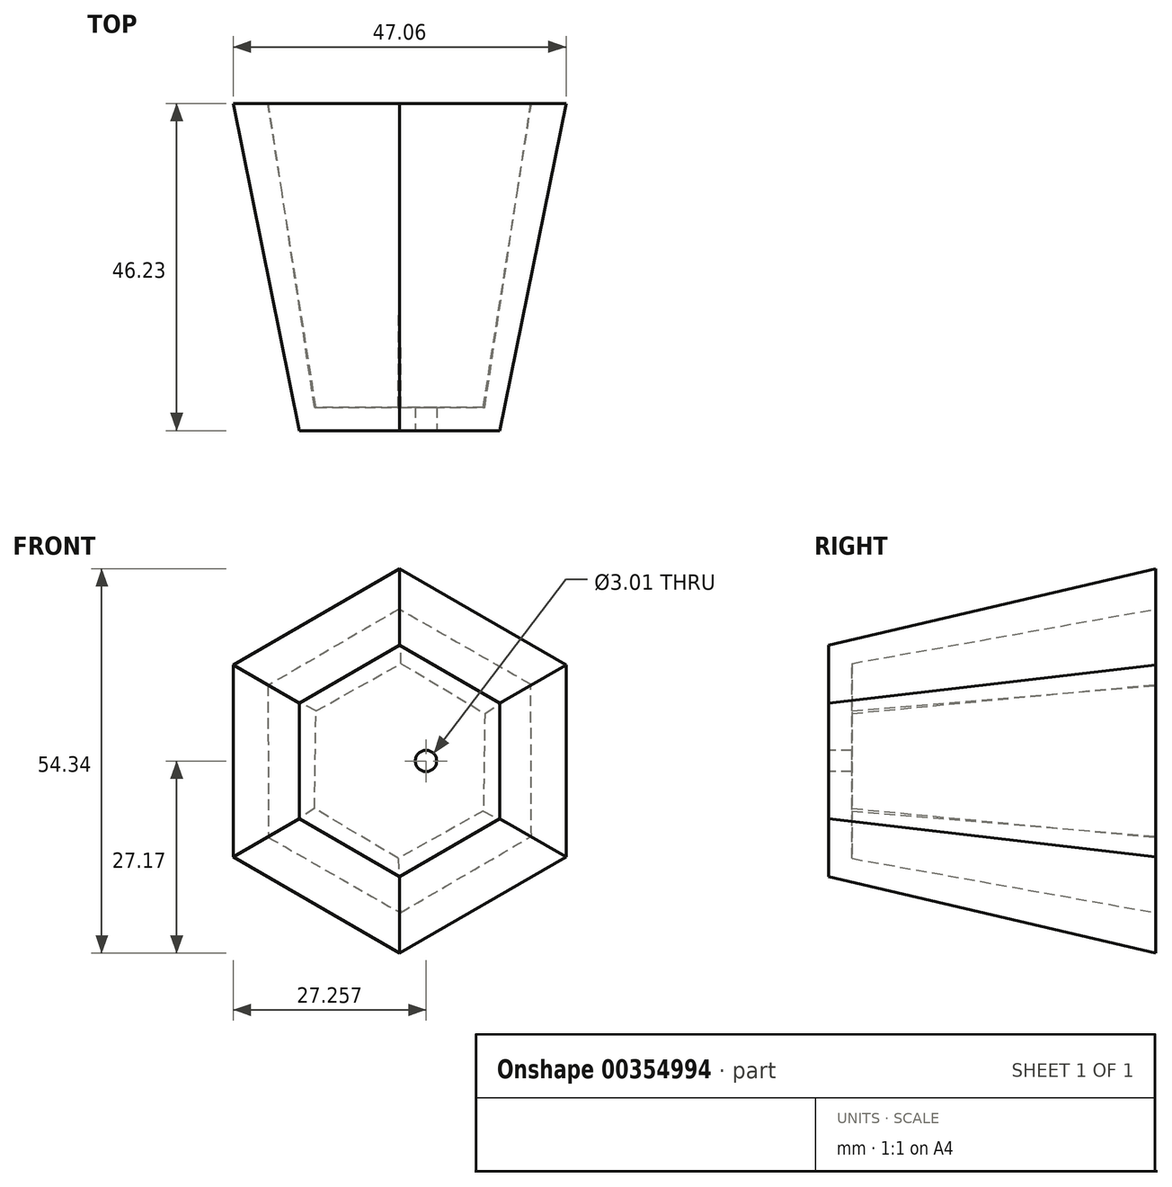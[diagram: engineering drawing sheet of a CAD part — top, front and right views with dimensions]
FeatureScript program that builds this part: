
annotation { "Feature Type Name" : "Feature", "Feature Type Description" : "" }
export const myFeature = defineFeature(function(context is Context, id is Id, definition is map)
    precondition{}
    {
        {
            var Q0;
            Q0=qCreatedBy(makeId("Front.planeOp"),FACE);
            var sketch = newSketch(context, id + "F0", { "sketchPlane" : qUnion([Q0])});
            skCircle(sketch, "E0.cCircle", {"center": v(0, 0) * mm, "radius": 23.53 * mm, "construction": true});
            skLineSegment(sketch, "E0.0", {"start": v(-23.53, -13.58) * mm, "end": v(-23.53, 13.58) * mm});
            skLineSegment(sketch, "E0.1", {"start": v(-23.53, 13.58) * mm, "end": v(0, 27.17) * mm});
            skLineSegment(sketch, "E0.2", {"start": v(0, 27.17) * mm, "end": v(23.53, 13.58) * mm});
            skLineSegment(sketch, "E0.3", {"start": v(23.53, 13.58) * mm, "end": v(23.53, -13.58) * mm});
            skLineSegment(sketch, "E0.4", {"start": v(23.53, -13.58) * mm, "end": v(0, -27.17) * mm});
            skLineSegment(sketch, "E0.5", {"start": v(0, -27.17) * mm, "end": v(-23.53, -13.58) * mm});
            skPoint(sketch, "E0.0.midPoint", {"position": v(-23.53, 0) * mm});
            skPoint(sketch, "E1.0.midPoint", {"position": v(-19.42, 0) * mm});
            skSolve(sketch);
        }
        {
            var Q0;
            Q0=qCreatedBy(makeId("Front.planeOp"),FACE);
            cPlane(context, id + "F1", {"entities" : qUnion([Q0]), "cplaneType" : CPlaneType.OFFSET, "offset" : 46.23 * mm, "width" : 152.4 * mm, "height" : 152.4 * mm});
        }
        {
            var Q0;
            Q0=qCreatedBy(id+"F1.planeOp",FACE);
            var sketch = newSketch(context, id + "F2", { "sketchPlane" : qUnion([Q0])});
            skCircle(sketch, "E2.cCircle", {"center": v(0, 0) * mm, "radius": 14.16 * mm, "construction": true});
            skLineSegment(sketch, "E2.0", {"start": v(0, 16.35) * mm, "end": v(14.17, 8.17) * mm});
            skLineSegment(sketch, "E2.1", {"start": v(14.17, 8.17) * mm, "end": v(14.16, -8.18) * mm});
            skLineSegment(sketch, "E2.2", {"start": v(14.16, -8.18) * mm, "end": v(0, -16.35) * mm});
            skLineSegment(sketch, "E2.3", {"start": v(0, -16.35) * mm, "end": v(-14.17, -8.17) * mm});
            skLineSegment(sketch, "E2.4", {"start": v(-14.17, -8.17) * mm, "end": v(-14.16, 8.18) * mm});
            skLineSegment(sketch, "E2.5", {"start": v(-14.16, 8.18) * mm, "end": v(0, 16.35) * mm});
            skPoint(sketch, "E2.0.midPoint", {"position": v(7.09, 12.26) * mm});
            skSolve(sketch);
        }
        {
            var Q0;
            Q0=makeQuery(id+"F0.imprint","IMPRINT",FACE,{"disambiguationData":[TD([[makeQuery(id+"F0.imprint","IMPRINT",EDGE,{"derivedFrom":sQuery(id+"F0.wireOp",EDGE,"E0.0")}),-1.0]])]});
            var Q1;
            Q1=makeQuery(id+"F2.imprint","IMPRINT",FACE,{"disambiguationData":[TD([[makeQuery(id+"F2.imprint","IMPRINT",EDGE,{"derivedFrom":sQuery(id+"F2.wireOp",EDGE,"E2.0")}),-1.0]])]});
            loft(context, id + "F3", {"sheetProfilesArray" : [{ "sheetProfileEntities" : qUnion([Q0]) }, { "sheetProfileEntities" : qUnion([Q1]) }]});
        }
        {
            var Q0;
            Q0=makeQuery(id+"F3.opLoft","CAP_FACE",FACE,{"disambiguationData":[OSD([makeQuery(id+"F0.imprint","IMPRINT",FACE,{"disambiguationData":[TD([[makeQuery(id+"F0.imprint","IMPRINT",EDGE,{"derivedFrom":sQuery(id+"F0.wireOp",EDGE,"E0.0")}),-1.0]])]})])],"isStart":true});
            cPlane(context, id + "F4", {"entities" : qUnion([Q0]), "cplaneType" : CPlaneType.OFFSET, "offset" : 1.78 * mm, "width" : 152.4 * mm, "height" : 152.4 * mm});
        }
        {
            var Q0;
            Q0=qCreatedBy(id+"F4.planeOp",FACE);
            var sketch = newSketch(context, id + "F5", { "sketchPlane" : qUnion([Q0])});
            skCircle(sketch, "E3.cCircle", {"center": v(0, 0) * mm, "radius": 18.85 * mm, "construction": true});
            skLineSegment(sketch, "E3.0", {"start": v(-18.8, 10.97) * mm, "end": v(0.1, 21.77) * mm});
            skLineSegment(sketch, "E3.1", {"start": v(0.1, 21.77) * mm, "end": v(18.9, 10.8) * mm});
            skLineSegment(sketch, "E3.2", {"start": v(18.9, 10.8) * mm, "end": v(18.8, -10.97) * mm});
            skLineSegment(sketch, "E3.3", {"start": v(18.8, -10.97) * mm, "end": v(-0.1, -21.77) * mm});
            skLineSegment(sketch, "E3.4", {"start": v(-0.1, -21.77) * mm, "end": v(-18.9, -10.8) * mm});
            skLineSegment(sketch, "E3.5", {"start": v(-18.9, -10.8) * mm, "end": v(-18.8, 10.97) * mm});
            skPoint(sketch, "E3.0.midPoint", {"position": v(-9.35, 16.37) * mm});
            skSolve(sketch);
        }
        {
            var Q0;
            Q0=makeQuery(id+"F3.opLoft","CAP_FACE",FACE,{"disambiguationData":[OSD([makeQuery(id+"F2.imprint","IMPRINT",FACE,{"disambiguationData":[TD([[makeQuery(id+"F2.imprint","IMPRINT",EDGE,{"derivedFrom":sQuery(id+"F2.wireOp",EDGE,"E2.0")}),-1.0]])]})])],"isStart":true});
            cPlane(context, id + "F6", {"entities" : qUnion([Q0]), "cplaneType" : CPlaneType.OFFSET, "offset" : 3.3 * mm, "oppositeDirection" : true, "width" : 152.4 * mm, "height" : 152.4 * mm});
        }
        {
            var Q0;
            Q0=qCreatedBy(id+"F6.planeOp",FACE);
            var sketch = newSketch(context, id + "F7", { "sketchPlane" : qUnion([Q0])});
            skCircle(sketch, "E4.cCircle", {"center": v(0, 0) * mm, "radius": 11.93 * mm, "construction": true});
            skLineSegment(sketch, "E4.0", {"start": v(-11.83, 7.06) * mm, "end": v(0.2, 13.77) * mm});
            skLineSegment(sketch, "E4.1", {"start": v(0.2, 13.77) * mm, "end": v(12.03, 6.71) * mm});
            skLineSegment(sketch, "E4.2", {"start": v(12.03, 6.71) * mm, "end": v(11.83, -7.06) * mm});
            skLineSegment(sketch, "E4.3", {"start": v(11.83, -7.06) * mm, "end": v(-0.2, -13.77) * mm});
            skLineSegment(sketch, "E4.4", {"start": v(-0.2, -13.77) * mm, "end": v(-12.03, -6.71) * mm});
            skLineSegment(sketch, "E4.5", {"start": v(-12.03, -6.71) * mm, "end": v(-11.83, 7.06) * mm});
            skPoint(sketch, "E4.0.midPoint", {"position": v(-5.81, 10.42) * mm});
            skSolve(sketch);
        }
        {
            var Q1;
            Q1 = qSketchRegion(id + "F7", true);
            var Q2;
            Q2=makeQuery(id+"F5.imprint","IMPRINT",FACE,{"disambiguationData":[TD([[makeQuery(id+"F5.imprint","IMPRINT",EDGE,{"derivedFrom":sQuery(id+"F5.wireOp",EDGE,"E3.0")}),-1.0]])]});
            loft(context, id + "F8", {"operationType" : NewBodyOperationType.REMOVE, "sheetProfilesArray" : [{ "sheetProfileEntities" : qUnion([Q1]) }, { "sheetProfileEntities" : qUnion([Q2]) }]});
        }
        {
            var Q0;
            Q0=makeQuery(id+"F3.opLoft","CAP_FACE",FACE,{"disambiguationData":[OSD([makeQuery(id+"F2.imprint","IMPRINT",FACE,{"disambiguationData":[TD([[makeQuery(id+"F2.imprint","IMPRINT",EDGE,{"derivedFrom":sQuery(id+"F2.wireOp",EDGE,"E2.0")}),-1.0]])]})])],"isStart":true});
            cPlane(context, id + "F9", {"entities" : qUnion([Q0]), "cplaneType" : CPlaneType.OFFSET, "offset" : 0 * mm, "width" : 152.4 * mm, "height" : 152.4 * mm});
        }
        {
            var Q0;
            Q0=qCreatedBy(id+"F9.planeOp",FACE);
            var sketch = newSketch(context, id + "F10", { "sketchPlane" : qUnion([Q0])});
            skCircle(sketch, "E5", {"center": v(3.73, 0) * mm, "radius": 1.5 * mm});
            skSolve(sketch);
        }
        {
            var Q0;
            Q0 = qSketchRegion(id + "F10", true);
            extrude(context, id + "F11", {"entities" : qUnion([Q0]), "operationType" : NewBodyOperationType.REMOVE, "oppositeDirection" : true, "depth" : 4.57 * mm});
        }
    });
